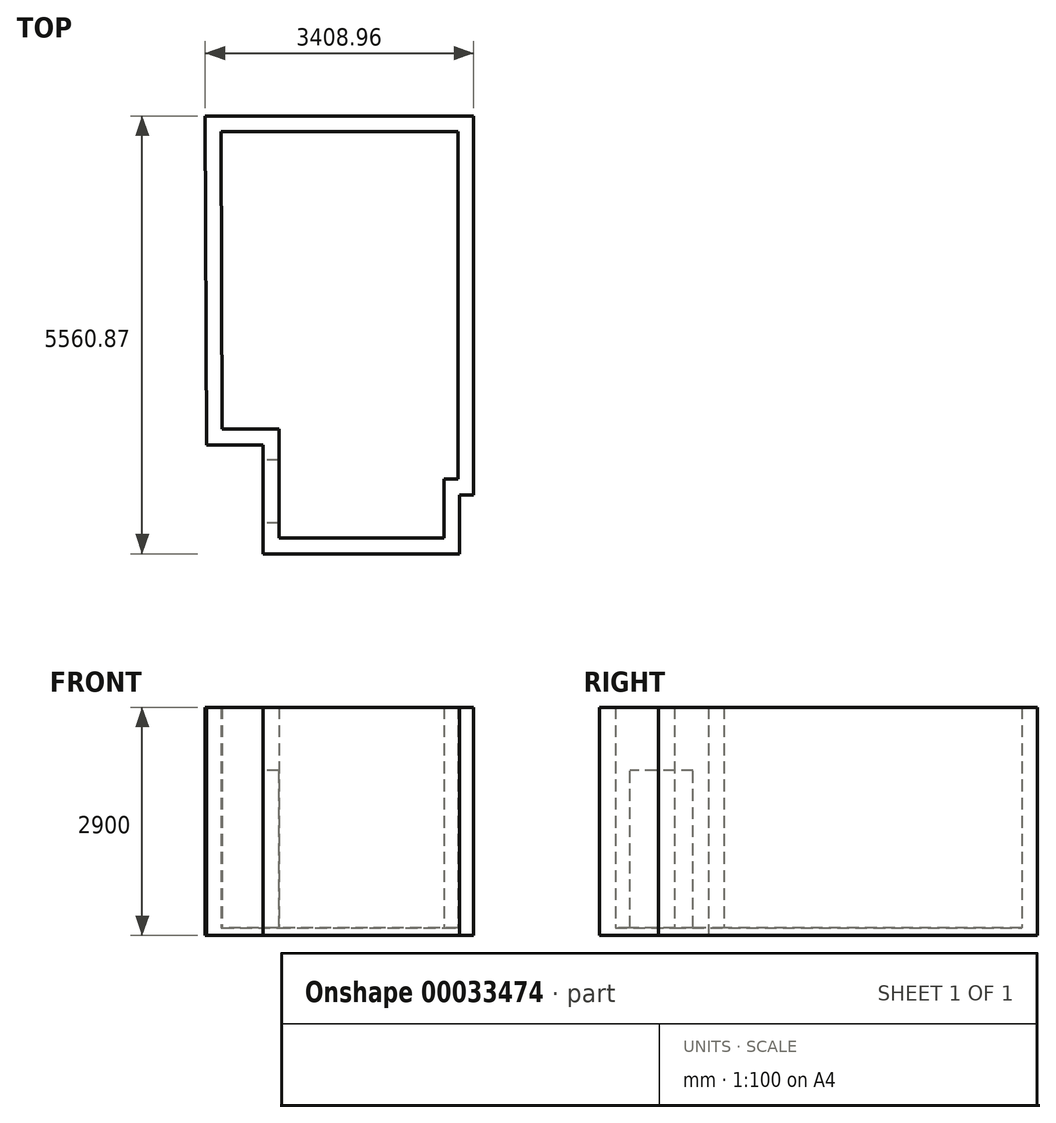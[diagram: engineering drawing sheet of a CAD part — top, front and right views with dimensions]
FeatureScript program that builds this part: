
annotation { "Feature Type Name" : "Feature", "Feature Type Description" : "" }
export const myFeature = defineFeature(function(context is Context, id is Id, definition is map)
    precondition{}
    {
        {
            var Q0;
            Q0=qCreatedBy(makeId("Top.planeOp"),FACE);
            var sketch = newSketch(context, id + "F0", { "sketchPlane" : qUnion([Q0])});
            skLineSegment(sketch, "E0", {"start": v(-1477.33, -3711.86) * mm, "end": v(-757.37, -3711.86) * mm});
            skLineSegment(sketch, "E1", {"start": v(-757.37, -3711.86) * mm, "end": v(-757.37, -5094.18) * mm});
            skLineSegment(sketch, "E2", {"start": v(-757.37, -5094.18) * mm, "end": v(1337.7, -5094.18) * mm});
            skLineSegment(sketch, "E3", {"start": v(1337.7, -5094.18) * mm, "end": v(1337.7, -4345.43) * mm});
            skLineSegment(sketch, "E4", {"start": v(1337.7, -4345.43) * mm, "end": v(1517.7, -4345.43) * mm});
            skLineSegment(sketch, "E5", {"start": v(1517.7, -4345.43) * mm, "end": v(1517.7, 67.91) * mm});
            skLineSegment(sketch, "E6", {"start": v(1517.7, 67.91) * mm, "end": v(-1491.73, 67.91) * mm});
            skLineSegment(sketch, "E7", {"start": v(-1491.73, 67.91) * mm, "end": v(-1477.33, -3711.86) * mm});
            skLineSegment(sketch, "E8.0", {"start": v(1537.1, -4544.81) * mm, "end": v(1717.08, -4544.81) * mm});
            skLineSegment(sketch, "E8.1", {"start": v(1537.1, -5293.57) * mm, "end": v(1537.1, -4544.81) * mm});
            skLineSegment(sketch, "E8.2", {"start": v(-956.76, -5293.57) * mm, "end": v(1537.1, -5293.57) * mm});
            skLineSegment(sketch, "E8.3", {"start": v(-956.76, -3911.25) * mm, "end": v(-956.76, -5293.57) * mm});
            skLineSegment(sketch, "E8.4", {"start": v(-1675.96, -3911.25) * mm, "end": v(-956.76, -3911.25) * mm});
            skLineSegment(sketch, "E8.5", {"start": v(1717.08, -4544.81) * mm, "end": v(1717.08, 267.3) * mm});
            skLineSegment(sketch, "E8.6", {"start": v(-1691.88, 267.3) * mm, "end": v(-1675.96, -3911.25) * mm});
            skLineSegment(sketch, "E8.7", {"start": v(1717.08, 267.3) * mm, "end": v(-1691.88, 267.3) * mm});
            skSolve(sketch);
        }
        {
            var Q0;
            Q0=makeQuery(id+"F0.imprint","IMPRINT",FACE,{"disambiguationData":[TD([[makeQuery(id+"F0.imprint","IMPRINT",EDGE,{"derivedFrom":sQuery(id+"F0.wireOp",EDGE,"E0")}),1.0]])]});
            extrude(context, id + "F1", {"entities" : qUnion([Q0]), "oppositeDirection" : true, "depth" : 25 * mm});
        }
        {
            var Q0;
            Q0=makeQuery(id+"F0.imprint","IMPRINT",FACE,{"disambiguationData":[TD([[makeQuery(id+"F0.imprint","IMPRINT",EDGE,{"derivedFrom":sQuery(id+"F0.wireOp",EDGE,"E0")}),-1.0]])]});
            extrude(context, id + "F2", {"entities" : qUnion([Q0]), "depth" : 2800 * mm});
        }
        {
            var Q0;
            Q0=makeQuery(id+"F2.opExtrude","SWEPT_FACE",FACE,{"disambiguationData":[OSD([sQuery(id+"F0.wireOp",EDGE,"E8.3")])]});
            var sketch = newSketch(context, id + "F3", { "sketchPlane" : qUnion([Q0])});
            skLineSegment(sketch, "E9.bottom", {"start": v(4105.52, 0) * mm, "end": v(4905.52, 0) * mm});
            skLineSegment(sketch, "E9.top", {"start": v(4105.52, 2000) * mm, "end": v(4905.52, 2000) * mm});
            skLineSegment(sketch, "E9.left", {"start": v(4105.52, 0) * mm, "end": v(4105.52, 2000) * mm});
            skLineSegment(sketch, "E9.right", {"start": v(4905.52, 0) * mm, "end": v(4905.52, 2000) * mm});
            skSolve(sketch);
        }
        {
            var Q0;
            Q0=makeQuery(id+"F3.imprint","IMPRINT",FACE,{"disambiguationData":[TD([[makeQuery(id+"F3.imprint","IMPRINT",EDGE,{"derivedFrom":sQuery(id+"F3.wireOp",EDGE,"E9.bottom")}),1.0]])]});
            extrude(context, id + "F4", {"entities" : qUnion([Q0]), "operationType" : NewBodyOperationType.REMOVE, "endBound" : BoundingType.UP_TO_NEXT, "oppositeDirection" : true, "depth" : 25 * mm});
        }
        {
            var Q0;
            Q0=makeQuery(id+"F0.imprint","IMPRINT",FACE,{"disambiguationData":[TD([[makeQuery(id+"F0.imprint","IMPRINT",EDGE,{"derivedFrom":sQuery(id+"F0.wireOp",EDGE,"E0")}),-1.0]])]});
            var Q1;
            Q1=makeQuery(id+"F0.imprint","IMPRINT",FACE,{"disambiguationData":[TD([[makeQuery(id+"F0.imprint","IMPRINT",EDGE,{"derivedFrom":sQuery(id+"F0.wireOp",EDGE,"E0")}),1.0]])]});
            extrude(context, id + "F5", {"entities" : qUnion([Q0, Q1]), "operationType" : NewBodyOperationType.ADD, "oppositeDirection" : true, "depth" : 100 * mm});
        }
    });
